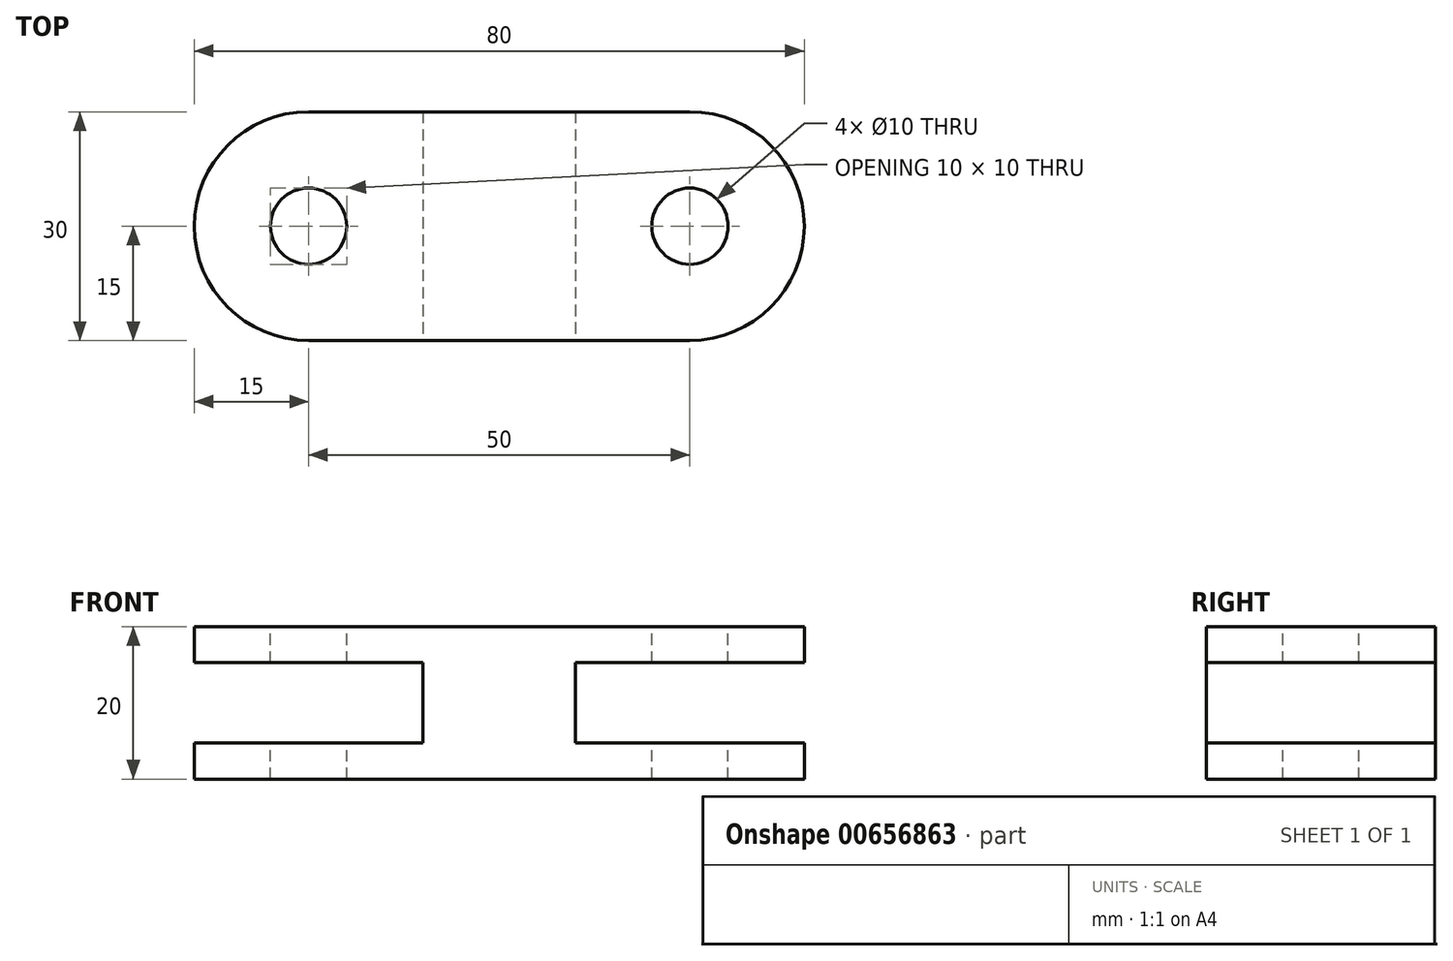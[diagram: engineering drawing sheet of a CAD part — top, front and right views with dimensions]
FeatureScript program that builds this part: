
annotation { "Feature Type Name" : "Feature", "Feature Type Description" : "" }
export const myFeature = defineFeature(function(context is Context, id is Id, definition is map)
    precondition{}
    {
        {
            var Q0;
            Q0=qCreatedBy(makeId("Top.planeOp"),FACE);
            var sketch = newSketch(context, id + "F0", { "sketchPlane" : qUnion([Q0])});
            skLineSegment(sketch, "E0.bottom", {"start": v(25, 15) * mm, "end": v(-25, 15) * mm});
            skLineSegment(sketch, "E0.top", {"start": v(25, -15) * mm, "end": v(-25, -15) * mm});
            skLineSegment(sketch, "E0.left", {"start": v(40, 0) * mm, "end": v(40, 0) * mm});
            skLineSegment(sketch, "E0.right", {"start": v(-40, 0) * mm, "end": v(-40, 0) * mm});
            skPoint(sketch, "E0.middle", {"position": v(0, 0) * mm});
            skPoint(sketch, "E1.visualSharp", {"position": v(-40, 15) * mm});
            skArc(sketch, "E1.filletArc", {"start": v(-25, 15) * mm, "mid": v(-35.6, 10.6) * mm, "end": v(-40, 0) * mm});
            skPoint(sketch, "E2.visualSharp", {"position": v(-40, -15) * mm});
            skArc(sketch, "E2.filletArc", {"start": v(-40, 0) * mm, "mid": v(-35.6, -10.6) * mm, "end": v(-25, -15) * mm});
            skPoint(sketch, "E3.visualSharp", {"position": v(40, -15) * mm});
            skArc(sketch, "E3.filletArc", {"start": v(25, -15) * mm, "mid": v(35.6, -10.6) * mm, "end": v(40, 0) * mm});
            skPoint(sketch, "E4.visualSharp", {"position": v(40, 15) * mm});
            skArc(sketch, "E4.filletArc", {"start": v(40, 0) * mm, "mid": v(35.6, 10.6) * mm, "end": v(25, 15) * mm});
            skSolve(sketch);
        }
        {
            var Q0;
            Q0 = qSketchRegion(id + "F0", true);
            extrude(context, id + "F1", {"entities" : qUnion([Q0]), "depth" : 20 * mm, "offsetDistance" : 25 * mm});
        }
        {
            var Q0;
            Q0=makeQuery(id+"F1.opExtrude","CAP_FACE",FACE,{"disambiguationData":[OSD([sQuery(id+"F0.wireOp",EDGE,"E0.bottom"),sQuery(id+"F0.wireOp",EDGE,"E0.top"),sQuery(id+"F0.wireOp",EDGE,"E1.filletArc"),sQuery(id+"F0.wireOp",EDGE,"E2.filletArc"),sQuery(id+"F0.wireOp",EDGE,"E3.filletArc"),sQuery(id+"F0.wireOp",EDGE,"E4.filletArc")])],"isStart":false});
            var sketch = newSketch(context, id + "F2", { "sketchPlane" : qUnion([Q0])});
            skCircle(sketch, "E5", {"center": v(25, 0) * mm, "radius": 5 * mm});
            skCircle(sketch, "E6", {"center": v(-25, 0) * mm, "radius": 5 * mm});
            skSolve(sketch);
        }
        {
            var Q0;
            Q0 = qSketchRegion(id + "F2", true);
            extrude(context, id + "F3", {"entities" : qUnion([Q0]), "operationType" : NewBodyOperationType.REMOVE, "oppositeDirection" : true, "depth" : 25 * mm, "offsetDistance" : 25 * mm});
        }
        {
            var Q0;
            Q0=makeQuery(id+"F1.opExtrude","SWEPT_FACE",FACE,{"disambiguationData":[OSD([sQuery(id+"F0.wireOp",EDGE,"E0.top")])]});
            var sketch = newSketch(context, id + "F4", { "sketchPlane" : qUnion([Q0])});
            skLineSegment(sketch, "E7.bottom", {"start": v(40, 15.25) * mm, "end": v(10, 15.25) * mm});
            skLineSegment(sketch, "E7.top", {"start": v(40, 4.75) * mm, "end": v(10, 4.75) * mm});
            skLineSegment(sketch, "E7.left", {"start": v(40, 15.25) * mm, "end": v(40, 4.75) * mm});
            skLineSegment(sketch, "E7.right", {"start": v(10, 15.25) * mm, "end": v(10, 4.75) * mm});
            skPoint(sketch, "E7.middle", {"position": v(25, 10) * mm});
            skLineSegment(sketch, "E8", {"start": v(0, 0) * mm, "end": v(0, 31.14) * mm, "construction": true});
            skLineSegment(sketch, "E9.MirrorCS", {"start": v(-10, 15.25) * mm, "end": v(-10, 4.75) * mm});
            skLineSegment(sketch, "E10.MirrorCS", {"start": v(-40, 15.25) * mm, "end": v(-10, 15.25) * mm});
            skLineSegment(sketch, "E11.MirrorCS", {"start": v(-40, 4.75) * mm, "end": v(-10, 4.75) * mm});
            skLineSegment(sketch, "E12.MirrorCS", {"start": v(-40, 15.25) * mm, "end": v(-40, 4.75) * mm});
            skSolve(sketch);
        }
        {
            var Q0;
            Q0 = qSketchRegion(id + "F4", true);
            extrude(context, id + "F5", {"entities" : qUnion([Q0]), "operationType" : NewBodyOperationType.REMOVE, "oppositeDirection" : true, "depth" : 30 * mm, "offsetDistance" : 25 * mm});
        }
    });
